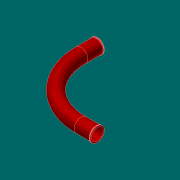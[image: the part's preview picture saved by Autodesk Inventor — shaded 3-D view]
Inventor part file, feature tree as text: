
AUTODESK INVENTOR PART (.ipt)
format: ipt  version: 2017.3 (Build 213256000, 256)  size: 172,544 bytes
history: native  units: in
note: dims shown in document units (in); Inventor stores cm internally (conversion verified against a paired STEP export)
features: sketch x7, extrude x6, projected_geometry x2, revolve x1, chamfer x1, fillet x1
ambient origin geometry x8: Origin, YZ Plane, XZ Plane, XY Plane, X Axis, Y Axis, Z Axis, Center Point
bodies: Solid1 (feature_tree)
feature tree (18):
  revolve  "Revolution1"  [1 undecoded]
  extrude  "Extrusion1"  TaperAngle=90.0deg  [1 undecoded]
  extrude  "Extrusion2"  TaperAngle=0.0deg  [1 undecoded]
  extrude  "Extrusion7"  TaperAngle=0.0deg  [1 undecoded]
  extrude  "Extrusion8"  Depth=1.0in TaperAngle=0.0deg
  chamfer  "Chamfer2"  [1 undecoded]
  extrude  "Extrusion4"  Depth=0.0312in
  extrude  "Extrusion6"  Depth=1.0in
  fillet  "Fillet2"  Radius=2.0in
  sketch  "Sketch1"  dims[d0=28.5in d1=32.5in]
  sketch  "Sketch2"  dims[d2=144.0in d3=90.0deg]
  projected_geometry  "Projected Loop1"
  sketch  "Sketch3"  dims[d4=38.7165in d5=0.0in]
  projected_geometry  "Projected Loop2"
  sketch  "Sketch5"  dims[d6=38.7165in d7=0.0in]
  sketch  "Sketch7"  dims[d11=34.23in d12=1.0in d13=0.0in]
  sketch  "Sketch8"  dims[d17=34.23in]
  sketch  "Sketch9"  dims[d18=1.0in d19=0.0in d24=0.0312in d25=34.5in d26=2.0in d27=0.0in d28=34.5in d29=2.0in d30=0.0in d31=1.0in d32=0.125in d33=45.0deg]
note: 5 required parameter values undecoded (feature->parameter linkage not recoverable at this tier; creation-order binding heuristic only, values carry confidence <= 0.55)